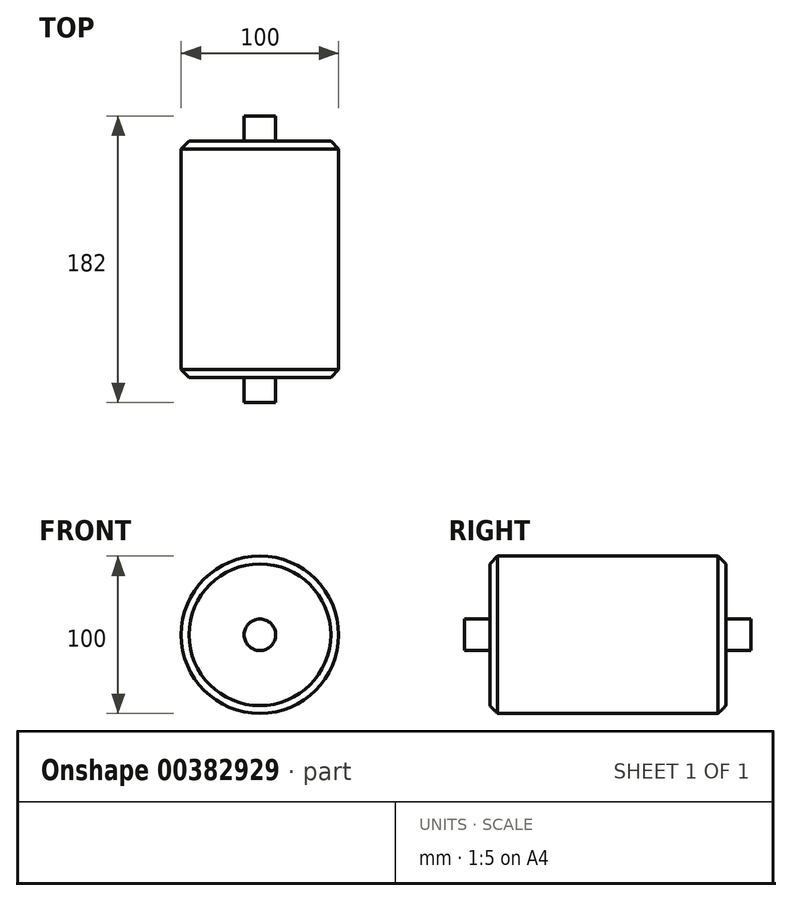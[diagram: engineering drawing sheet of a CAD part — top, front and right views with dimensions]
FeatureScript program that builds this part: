
annotation { "Feature Type Name" : "Feature", "Feature Type Description" : "" }
export const myFeature = defineFeature(function(context is Context, id is Id, definition is map)
    precondition{}
    {
        {
            var Q0;
            Q0=qCreatedBy(makeId("Right.planeOp"),FACE);
            var sketch = newSketch(context, id + "F0", { "sketchPlane" : qUnion([Q0])});
            skLineSegment(sketch, "E0", {"start": v(-89.68, 0) * mm, "end": v(92.32, 0) * mm, "construction": true});
            skLineSegment(sketch, "E1.bottom", {"start": v(-89.68, 0) * mm, "end": v(-73.68, 0) * mm});
            skLineSegment(sketch, "E1.top", {"start": v(-89.68, 10) * mm, "end": v(-73.68, 10) * mm});
            skLineSegment(sketch, "E1.left", {"start": v(-89.68, 0) * mm, "end": v(-89.68, 10) * mm});
            skLineSegment(sketch, "E1.right", {"start": v(-73.68, 0) * mm, "end": v(-73.68, 10) * mm});
            skLineSegment(sketch, "E2.bottom", {"start": v(-73.68, 0) * mm, "end": v(76.32, 0) * mm});
            skLineSegment(sketch, "E2.top", {"start": v(-73.68, 50) * mm, "end": v(76.32, 50) * mm});
            skLineSegment(sketch, "E2.left", {"start": v(-73.68, 0) * mm, "end": v(-73.68, 50) * mm});
            skLineSegment(sketch, "E2.right", {"start": v(76.32, 0) * mm, "end": v(76.32, 50) * mm});
            skLineSegment(sketch, "E3.bottom", {"start": v(76.32, 0) * mm, "end": v(92.32, 0) * mm});
            skLineSegment(sketch, "E3.top", {"start": v(76.32, 10) * mm, "end": v(92.32, 10) * mm});
            skLineSegment(sketch, "E3.left", {"start": v(76.32, 0) * mm, "end": v(76.32, 10) * mm});
            skLineSegment(sketch, "E3.right", {"start": v(92.32, 0) * mm, "end": v(92.32, 10) * mm});
            skSolve(sketch);
        }
        {
            var Q0;
            {var subQ0=sQuery(id+"F0.wireOp",EDGE,"E1.bottom");Q0=makeQuery(id+"F0.imprint","IMPRINT",FACE,{"disambiguationData":[TD([[makeQuery(id+"F0.imprint","IMPRINT",EDGE,{"derivedFrom":subQ0}),1.0]])]});}
            var Q1;
            {var subQ3=sQuery(id+"F0.wireOp",EDGE,"E2.bottom");Q1=makeQuery(id+"F0.imprint","IMPRINT",FACE,{"disambiguationData":[TD([[makeQuery(id+"F0.imprint","IMPRINT",EDGE,{"derivedFrom":subQ3}),1.0]])]});}
            var Q2;
            Q2=makeQuery(id+"F0.imprint","IMPRINT",FACE,{"disambiguationData":[TD([[makeQuery(id+"F0.imprint","IMPRINT",EDGE,{"derivedFrom":sQuery(id+"F0.wireOp",EDGE,"E3.bottom")}),1.0]])]});
            var Q3;
            Q3=sQuery(id+"F0.wireOp",EDGE,"E2.bottom");
            revolve(context, id + "F1", {"entities" : qUnion([Q0, Q1, Q2]), "axis" : qUnion([Q3]), "revolveType" : RevolveType.FULL});
        }
        {
            var Q0;
            Q0=makeQuery(id+"F1.opRevolve","SWEPT_EDGE",EDGE,{"disambiguationData":[OSD([sQuery(id+"F0.wireOp",EDGE,"E2.top"),sQuery(id+"F0.wireOp",EDGE,"E2.left")])]});
            var Q1;
            Q1=makeQuery(id+"F1.opRevolve","SWEPT_EDGE",EDGE,{"disambiguationData":[OSD([sQuery(id+"F0.wireOp",EDGE,"E2.top"),sQuery(id+"F0.wireOp",EDGE,"E2.right")])]});
            chamfer(context, id + "F2", {"entities" : qUnion([Q0, Q1]), "chamferType" : ChamferType.OFFSET_ANGLE, "width" : 5 * mm, "oppositeDirection" : false, "angle" : 45 * degree, "tangentPropagation" : true});
        }
    });
